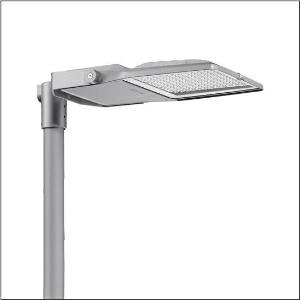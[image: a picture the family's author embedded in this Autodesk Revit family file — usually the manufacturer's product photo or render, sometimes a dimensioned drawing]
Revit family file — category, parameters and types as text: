
# Revit family: floodlight_fl_21_iq_midi___pl61_5xa7782e2c3a_85c4
name_source: partatom
category: Lighting Fixtures
units: mm (PartAtom-declared; Revit-internal decimal feet)

## family parameters
Cut with Voids When Loaded = No
Host = Face
Light Source = No
Part Type = Normal
Room Calculation Point = No
Round Connector Dimension = Use Diameter
Shared = No

## types (1)
- --- (1 x LED, 26360 lm, 208.1 W, 3000K)
    Apparent Load = 208 VA
    CIE Flux Codes = 33 65 98 100 100
    Color Rendering = 70
    Color Temperature = 3000K
    Default Elevation = 1800 mm
    Description = Floodlight FL 21 iQ midi, floodlight, primary light control with lens, of PMMA, primary optical cover: protective disc, of toughened safety glass, transparent, light distribution: PL61, light emission: direct distribution, installation type: surface-mounted, LED, High Power LED, rated luminous flux: 26.360lm, luminous efficacy: 127lm/W, light colour: 730, colour temperature: 3000K, control gear: ECG iQ, control: optimised constant luminous flux control (CLO 2.0), Desk-Remote (wireless, voltage-free reading and setting of iQ features in the workshop via application-optimized NFC function/RFID function), Smart-Wire, Night-Set, Temp-Guard, Auto-Match, Street-Remote, with terminal, 6-pole, mains connection: 220..240V, AC, 50/60Hz, start of lifetime: 208W, end of service life: 227W, reduction: 90W, luminaire housing, of diecast aluminium, powder-coated, Siteco® metallic grey (DB 702S), corrosivity category C5 mid according to DIN EN ISO 12944, sealing non-destructively replaceable, please order mast flange separately, mast bracket, of steel, galvanised, powder-coated, Siteco® metallic grey (DB 702S), protection rating (complete): IP66, insulation class (complete): insulation class II (safety insulation), certification: CE, protection symbol: D, impact resistance: IK08, permissible operating ambient temperature: -40..+40°C, permissible operating ambient temperature for outdoor applications: -40..+50°C, standard: DIN EN 12944, LABS conformity tested according to VDMA 24364:2018-05, packaging unit: 1 piece

Light Distribution: PL61
    Height = 76 mm
    Lamp = 1 x LED
    Lamp Light Flux = 26360 lm
    Lamp Power = 208.1 W
    Lamp count = 1
    Length = 657 mm
    Luminous efficacy = 127 lm/W
    Manufacturer = Siteco
    ModVariant = No
    Model = 5XA7782E2C3A
    Number of Poles = 1
    OnlyDefault = Yes
    Power Factor = 1
    Product Name = Floodlight FL 21 iQ midi | PL61
    Product group = floodlight | pylon annexe
    ProductGroupID = 6200
    Protection Class = Protection class II
    Protection Degree = IP 66
    RLX_Detail_Level = 1
    RLX_Emergency_Light_Flux = 0 lm
    RLX_Emergency_Type = 0
    RLX_Emergency_Type_DB = No
    RlxData = <blob elided: 153601 chars, md5=f4d098f9>
    Socket = socket
    Standby Power = 0 W
    System Light Flux = 26360 lm
    System Power = 208 W
    Type Comments = factory setting: luminous flux: 100 % | dim-lin: 254 | 710 mA
    Type Image = l_1007123.jpg
    URL = http://relux.com
    VarID = @adj_038875
    Voltage = 0 V
    Weight = 0.00 kg
    Width = 442 mm

## geometry (parser evidence)
native form markers: Blend x4, Sweep x13
no freeform markers — native parametric forms only
